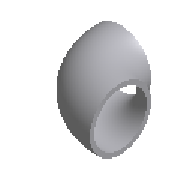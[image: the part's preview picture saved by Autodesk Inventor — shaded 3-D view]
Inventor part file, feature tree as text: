
AUTODESK INVENTOR PART (.ipt)
format: ipt  version: 2023 (Build 270158000, 158)  size: 190,976 bytes
history: native  units: mm (DEFAULTED — no unit token found)
features: other x4, sketch x2, sweep x1
ambient origin geometry x8: Origin, YZ Plane, XZ Plane, XY Plane, X Axis, Y Axis, Z Axis, Center Point
bodies: Solid1 (feature_tree)
feature tree (7):
  sweep  "Sweep1"
  other  "Work Point1"
  other  "Work Point2"
  other  "Work Axis1"
  other  "Work Axis2"
  sketch  "Sketch1"  dims[d0=318.1mm d1=323.9mm]
  sketch  "Sketch2"  dims[d2=305.0mm d3=305.0mm d4=0.0mm d5=0.0mm]
